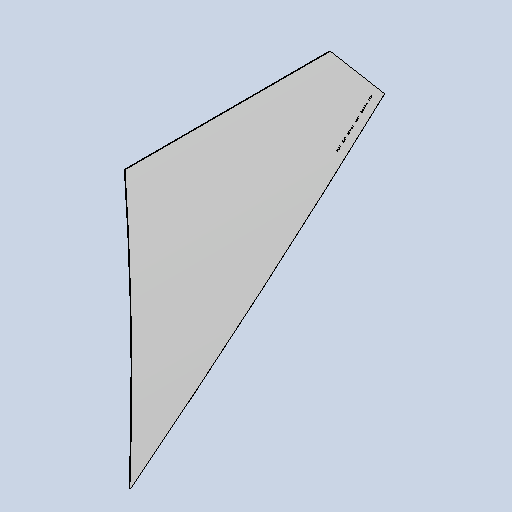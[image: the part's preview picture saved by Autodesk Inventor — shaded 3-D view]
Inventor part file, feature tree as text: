
AUTODESK INVENTOR PART (.ipt)
format: ipt  version: 2025 (Build 290162010, 162A)  size: 504,832 bytes
history: native  units: mm
features: sheet_metal_op x3, other x3, sketch x3, extrude x1, fillet x1, projected_geometry x1
ambient origin geometry x8: Origin, YZ Plane, XZ Plane, XY Plane, X Axis, Y Axis, Z Axis, Center Point
bodies: Body1 (feature_tree)
feature tree (12):
  sheet_metal_op  "Contour Flange2"
  extrude  "Extrusion2"  Depth=3.0mm
  fillet  "Fillet1"  Radius=1.5mm
  other  "Mark1"
  sketch  "Sketch1"  dims[d36=3.0mm d37=3.0mm d38=1.5mm]
  other  "Plate2"
  sheet_metal_op  "Bend2"
  sheet_metal_op  "Corner2"
  sketch  "Sketch2"  dims[d39=6.0mm]
  projected_geometry  "Projected Loop1"
  sketch  "Sketch3"  dims[d40=5.0mm d41=1250.0mm d42=5.0mm d43=3.0mm d44=12.0mm d45=3.0mm d46=5.0mm d54=1500.0mm d55=2700.0mm d58=2100.0mm d65=8.0mm d66=8.0mm d68=8.0mm d69=3.0mm d70=3.0mm d75=3.0mm d78=3.0mm d80=3.0mm d83=8.0mm d86=3.0mm d112=241.9mm d113=50.0mm d114=50.0mm d115=3.0mm d116=25.0mm d117=110.0mm d118=25.0mm d119=92.8mm d130=0.0mm d131=0.0mm d132=8.726646mm d133=1286.0mm d134=3.0mm d135=290.0mm d137=12.0mm d138=200.0mm d139=50.0mm d140=50.0mm]
  other  "Definition1"
